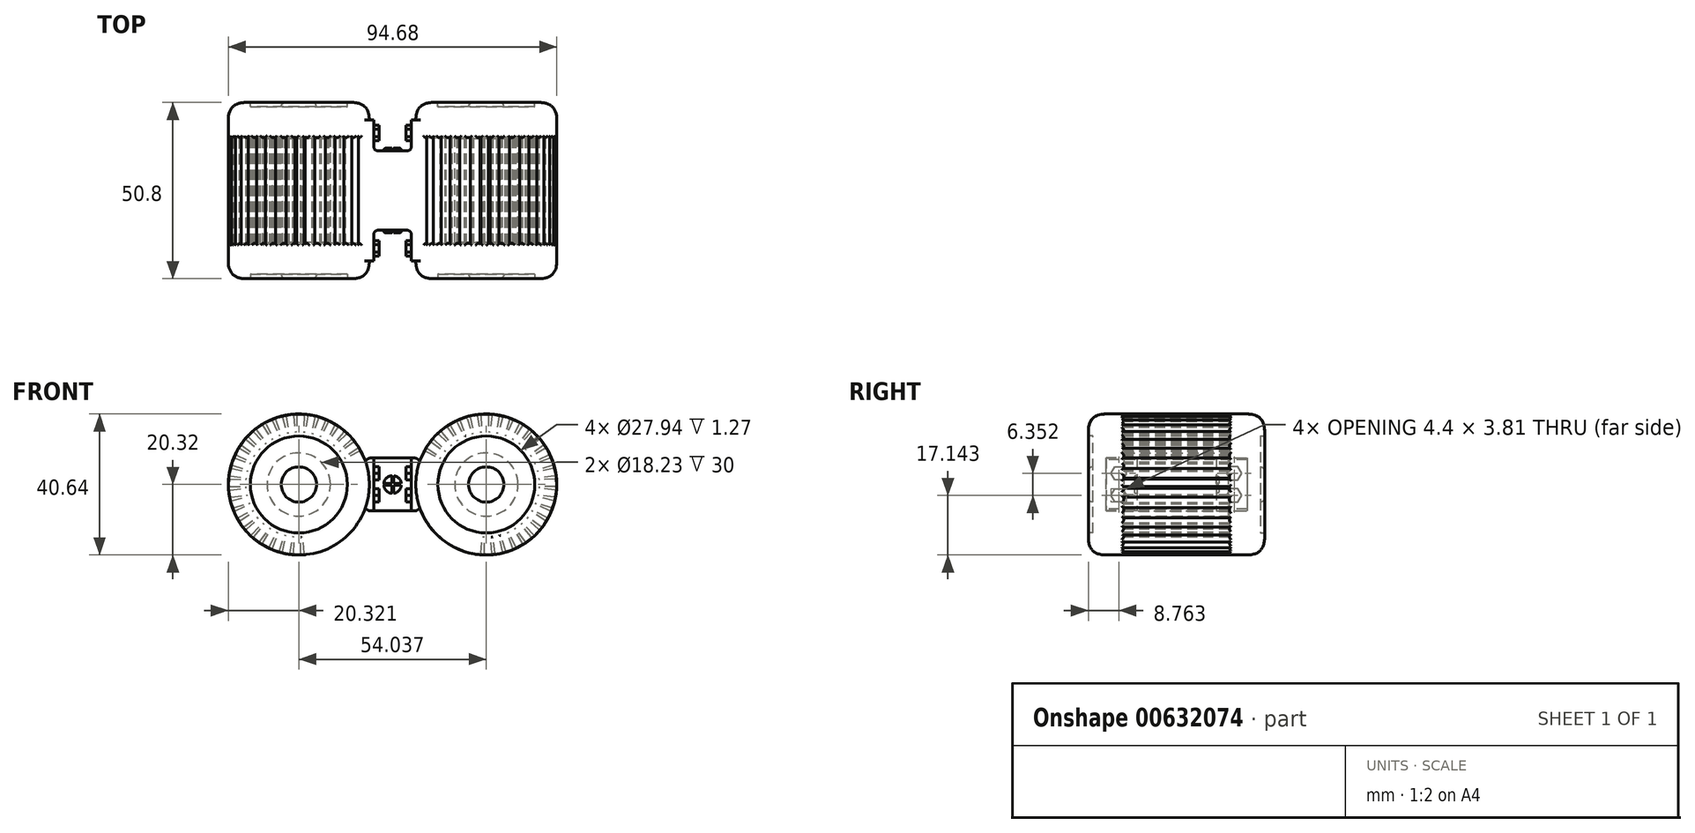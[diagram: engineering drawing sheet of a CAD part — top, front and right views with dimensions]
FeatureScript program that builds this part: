
annotation { "Feature Type Name" : "Feature", "Feature Type Description" : "" }
export const myFeature = defineFeature(function(context is Context, id is Id, definition is map)
    precondition{}
    {
        {
            var Q0;
            Q0=qCreatedBy(makeId("Front.planeOp"),FACE);
            var sketch = newSketch(context, id + "F0", { "sketchPlane" : qUnion([Q0])});
            skArc(sketch, "E0", {"start": v(26.53, 38.5) * mm, "mid": v(31.42, 78.66) * mm, "end": v(18.88, 40.2) * mm});
            skCircle(sketch, "E1", {"center": v(-27.02, 58.82) * mm, "radius": 20.32 * mm});
            skArc(sketch, "E2", {"start": v(18.88, 40.2) * mm, "mid": v(22.62, 38.98) * mm, "end": v(26.53, 38.5) * mm});
            skSolve(sketch);
        }
        {
            var Q0;
            Q0=qSketchRegion(id+"F0",true);
            extrude(context, id + "F1", {"entities" : qUnion([Q0]), "endBound" : BoundingType.SYMMETRIC, "depth" : 50.8 * mm});
        }
        {
            var Q0;
            Q0=qCreatedBy(makeId("Front.planeOp"),FACE);
            var sketch = newSketch(context, id + "F2", { "sketchPlane" : qUnion([Q0])});
            skLineSegment(sketch, "E3.1.0", {"start": v(13.83, 74.28) * mm, "end": v(17.03, 70.33) * mm});
            skLineSegment(sketch, "E3.1.1", {"start": v(13.07, 73.6) * mm, "end": v(16.65, 69.99) * mm});
            skLineSegment(sketch, "E3.1.2", {"start": v(13.07, 73.6) * mm, "end": v(13.83, 74.28) * mm});
            skLineSegment(sketch, "E3.1.3", {"start": v(16.65, 69.99) * mm, "end": v(17.03, 70.33) * mm, "construction": true});
            skLineSegment(sketch, "E3.1.4", {"start": v(16.65, 69.99) * mm, "end": v(17.03, 70.33) * mm});
            skPoint(sketch, "E4", {"position": v(27.02, 58.82) * mm});
            skPoint(sketch, "E5", {"position": v(-27.02, 58.82) * mm});
            skLineSegment(sketch, "E6", {"start": v(27.02, 58.82) * mm, "end": v(13.45, 73.94) * mm, "construction": true});
            skLineSegment(sketch, "E7.1.0", {"start": v(-13.07, 73.6) * mm, "end": v(-16.65, 69.99) * mm});
            skLineSegment(sketch, "E7.1.1", {"start": v(-13.83, 74.28) * mm, "end": v(-17.03, 70.33) * mm});
            skLineSegment(sketch, "E7.1.2", {"start": v(-13.83, 74.28) * mm, "end": v(-13.07, 73.6) * mm});
            skLineSegment(sketch, "E7.1.3", {"start": v(-17.03, 70.33) * mm, "end": v(-16.65, 69.99) * mm, "construction": true});
            skLineSegment(sketch, "E7.1.4", {"start": v(-17.03, 70.33) * mm, "end": v(-16.65, 69.99) * mm});
            skLineSegment(sketch, "E8", {"start": v(-27.02, 58.82) * mm, "end": v(-13.45, 73.94) * mm, "construction": true});
            skLineSegment(sketch, "E9.1.0", {"start": v(11.57, 72.03) * mm, "end": v(15.35, 68.63) * mm});
            skLineSegment(sketch, "E9.1.1", {"start": v(10.93, 71.24) * mm, "end": v(15.03, 68.23) * mm});
            skLineSegment(sketch, "E9.1.2", {"start": v(10.93, 71.24) * mm, "end": v(11.57, 72.03) * mm});
            skLineSegment(sketch, "E9.1.3", {"start": v(15.03, 68.23) * mm, "end": v(15.35, 68.63) * mm, "construction": true});
            skLineSegment(sketch, "E9.1.4", {"start": v(15.03, 68.23) * mm, "end": v(15.35, 68.63) * mm});
            skLineSegment(sketch, "E9.2.0", {"start": v(9.7, 69.45) * mm, "end": v(13.96, 66.68) * mm});
            skLineSegment(sketch, "E9.2.1", {"start": v(9.18, 68.57) * mm, "end": v(13.7, 66.24) * mm});
            skLineSegment(sketch, "E9.2.2", {"start": v(9.18, 68.57) * mm, "end": v(9.7, 69.45) * mm});
            skLineSegment(sketch, "E9.2.3", {"start": v(13.7, 66.24) * mm, "end": v(13.96, 66.68) * mm, "construction": true});
            skLineSegment(sketch, "E9.2.4", {"start": v(13.7, 66.24) * mm, "end": v(13.96, 66.68) * mm});
            skLineSegment(sketch, "E9.15.0", {"start": v(25.41, 38.55) * mm, "end": v(25.94, 43.62) * mm});
            skLineSegment(sketch, "E9.15.1", {"start": v(26.43, 38.5) * mm, "end": v(26.45, 43.59) * mm});
            skLineSegment(sketch, "E9.15.2", {"start": v(26.43, 38.5) * mm, "end": v(25.41, 38.55) * mm});
            skLineSegment(sketch, "E9.15.3", {"start": v(26.45, 43.59) * mm, "end": v(25.94, 43.62) * mm, "construction": true});
            skLineSegment(sketch, "E9.15.4", {"start": v(26.45, 43.59) * mm, "end": v(25.94, 43.62) * mm});
            skLineSegment(sketch, "E9.16.0", {"start": v(28.6, 38.55) * mm, "end": v(28.33, 43.63) * mm});
            skLineSegment(sketch, "E9.16.1", {"start": v(29.61, 38.66) * mm, "end": v(28.84, 43.69) * mm});
            skLineSegment(sketch, "E9.16.2", {"start": v(29.61, 38.66) * mm, "end": v(28.6, 38.55) * mm});
            skLineSegment(sketch, "E9.16.3", {"start": v(28.84, 43.69) * mm, "end": v(28.33, 43.63) * mm, "construction": true});
            skLineSegment(sketch, "E9.16.4", {"start": v(28.84, 43.69) * mm, "end": v(28.33, 43.63) * mm});
            skLineSegment(sketch, "E9.17.0", {"start": v(31.75, 39.05) * mm, "end": v(30.7, 44.03) * mm});
            skLineSegment(sketch, "E9.17.1", {"start": v(32.73, 39.31) * mm, "end": v(31.18, 44.16) * mm});
            skLineSegment(sketch, "E9.17.2", {"start": v(32.73, 39.31) * mm, "end": v(31.75, 39.05) * mm});
            skLineSegment(sketch, "E9.17.3", {"start": v(31.18, 44.16) * mm, "end": v(30.7, 44.03) * mm, "construction": true});
            skLineSegment(sketch, "E9.17.4", {"start": v(31.18, 44.16) * mm, "end": v(30.7, 44.03) * mm});
            skLineSegment(sketch, "E9.18.0", {"start": v(34.79, 40.03) * mm, "end": v(32.96, 44.78) * mm});
            skLineSegment(sketch, "E9.18.1", {"start": v(35.72, 40.45) * mm, "end": v(33.42, 44.99) * mm});
            skLineSegment(sketch, "E9.18.2", {"start": v(35.72, 40.45) * mm, "end": v(34.79, 40.03) * mm});
            skLineSegment(sketch, "E9.18.3", {"start": v(33.42, 44.99) * mm, "end": v(32.96, 44.78) * mm, "construction": true});
            skLineSegment(sketch, "E9.18.4", {"start": v(33.42, 44.99) * mm, "end": v(32.96, 44.78) * mm});
            skLineSegment(sketch, "E9.19.0", {"start": v(37.63, 41.48) * mm, "end": v(35.08, 45.89) * mm});
            skLineSegment(sketch, "E9.19.1", {"start": v(38.48, 42.03) * mm, "end": v(35.5, 46.16) * mm});
            skLineSegment(sketch, "E9.19.2", {"start": v(38.48, 42.03) * mm, "end": v(37.63, 41.48) * mm});
            skLineSegment(sketch, "E9.19.3", {"start": v(35.5, 46.16) * mm, "end": v(35.08, 45.89) * mm, "construction": true});
            skLineSegment(sketch, "E9.19.4", {"start": v(35.5, 46.16) * mm, "end": v(35.08, 45.89) * mm});
            skLineSegment(sketch, "E9.20.0", {"start": v(40.21, 43.35) * mm, "end": v(37, 47.3) * mm});
            skLineSegment(sketch, "E9.20.1", {"start": v(40.97, 44.03) * mm, "end": v(37.38, 47.65) * mm});
            skLineSegment(sketch, "E9.20.2", {"start": v(40.97, 44.03) * mm, "end": v(40.21, 43.35) * mm});
            skLineSegment(sketch, "E9.20.3", {"start": v(37.38, 47.65) * mm, "end": v(37, 47.3) * mm, "construction": true});
            skLineSegment(sketch, "E9.20.4", {"start": v(37.38, 47.65) * mm, "end": v(37, 47.3) * mm});
            skLineSegment(sketch, "E9.21.0", {"start": v(42.47, 45.6) * mm, "end": v(38.68, 49.01) * mm});
            skLineSegment(sketch, "E9.21.1", {"start": v(43.1, 46.4) * mm, "end": v(39, 49.4) * mm});
            skLineSegment(sketch, "E9.21.2", {"start": v(43.1, 46.4) * mm, "end": v(42.47, 45.6) * mm});
            skLineSegment(sketch, "E9.21.3", {"start": v(39, 49.4) * mm, "end": v(38.68, 49.01) * mm, "construction": true});
            skLineSegment(sketch, "E9.21.4", {"start": v(39, 49.4) * mm, "end": v(38.68, 49.01) * mm});
            skLineSegment(sketch, "E9.22.0", {"start": v(44.34, 48.19) * mm, "end": v(40.07, 50.96) * mm});
            skLineSegment(sketch, "E9.22.1", {"start": v(44.85, 49.07) * mm, "end": v(40.33, 51.4) * mm});
            skLineSegment(sketch, "E9.22.2", {"start": v(44.85, 49.07) * mm, "end": v(44.34, 48.19) * mm});
            skLineSegment(sketch, "E9.22.3", {"start": v(40.33, 51.4) * mm, "end": v(40.07, 50.96) * mm, "construction": true});
            skLineSegment(sketch, "E9.22.4", {"start": v(40.33, 51.4) * mm, "end": v(40.07, 50.96) * mm});
            skLineSegment(sketch, "E9.23.0", {"start": v(45.8, 51.03) * mm, "end": v(41.14, 53.1) * mm});
            skLineSegment(sketch, "E9.23.1", {"start": v(46.16, 51.98) * mm, "end": v(41.33, 53.57) * mm});
            skLineSegment(sketch, "E9.23.2", {"start": v(46.16, 51.98) * mm, "end": v(45.8, 51.03) * mm});
            skLineSegment(sketch, "E9.23.3", {"start": v(41.33, 53.57) * mm, "end": v(41.14, 53.1) * mm, "construction": true});
            skLineSegment(sketch, "E9.23.4", {"start": v(41.33, 53.57) * mm, "end": v(41.14, 53.1) * mm});
            skLineSegment(sketch, "E9.24.0", {"start": v(46.78, 54.06) * mm, "end": v(41.86, 55.37) * mm});
            skLineSegment(sketch, "E9.24.1", {"start": v(47, 55.05) * mm, "end": v(41.97, 55.87) * mm});
            skLineSegment(sketch, "E9.24.2", {"start": v(47, 55.05) * mm, "end": v(46.78, 54.06) * mm});
            skLineSegment(sketch, "E9.24.3", {"start": v(41.97, 55.87) * mm, "end": v(41.86, 55.37) * mm, "construction": true});
            skLineSegment(sketch, "E9.24.4", {"start": v(41.97, 55.87) * mm, "end": v(41.86, 55.37) * mm});
            skLineSegment(sketch, "E9.25.0", {"start": v(47.28, 57.21) * mm, "end": v(42.22, 57.74) * mm});
            skLineSegment(sketch, "E9.25.1", {"start": v(47.34, 58.23) * mm, "end": v(42.25, 58.25) * mm});
            skLineSegment(sketch, "E9.25.2", {"start": v(47.34, 58.23) * mm, "end": v(47.28, 57.21) * mm});
            skLineSegment(sketch, "E9.25.3", {"start": v(42.25, 58.25) * mm, "end": v(42.22, 57.74) * mm, "construction": true});
            skLineSegment(sketch, "E9.25.4", {"start": v(42.25, 58.25) * mm, "end": v(42.22, 57.74) * mm});
            skLineSegment(sketch, "E9.26.0", {"start": v(47.28, 60.4) * mm, "end": v(42.2, 60.13) * mm});
            skLineSegment(sketch, "E9.26.1", {"start": v(47.18, 61.41) * mm, "end": v(42.15, 60.64) * mm});
            skLineSegment(sketch, "E9.26.2", {"start": v(47.18, 61.41) * mm, "end": v(47.28, 60.4) * mm});
            skLineSegment(sketch, "E9.26.3", {"start": v(42.15, 60.64) * mm, "end": v(42.2, 60.13) * mm, "construction": true});
            skLineSegment(sketch, "E9.26.4", {"start": v(42.15, 60.64) * mm, "end": v(42.2, 60.13) * mm});
            skLineSegment(sketch, "E9.27.0", {"start": v(46.79, 63.55) * mm, "end": v(41.8, 62.5) * mm});
            skLineSegment(sketch, "E9.27.1", {"start": v(46.52, 64.53) * mm, "end": v(41.68, 62.98) * mm});
            skLineSegment(sketch, "E9.27.2", {"start": v(46.52, 64.53) * mm, "end": v(46.79, 63.55) * mm});
            skLineSegment(sketch, "E9.27.3", {"start": v(41.68, 62.98) * mm, "end": v(41.8, 62.5) * mm, "construction": true});
            skLineSegment(sketch, "E9.27.4", {"start": v(41.68, 62.98) * mm, "end": v(41.8, 62.5) * mm});
            skLineSegment(sketch, "E9.28.0", {"start": v(45.8, 66.59) * mm, "end": v(41.05, 64.76) * mm});
            skLineSegment(sketch, "E9.28.1", {"start": v(45.4, 67.51) * mm, "end": v(40.85, 65.22) * mm});
            skLineSegment(sketch, "E9.28.2", {"start": v(45.4, 67.51) * mm, "end": v(45.8, 66.59) * mm});
            skLineSegment(sketch, "E9.28.3", {"start": v(40.85, 65.22) * mm, "end": v(41.05, 64.76) * mm, "construction": true});
            skLineSegment(sketch, "E9.28.4", {"start": v(40.85, 65.22) * mm, "end": v(41.05, 64.76) * mm});
            skLineSegment(sketch, "E9.29.0", {"start": v(44.36, 69.43) * mm, "end": v(39.95, 66.88) * mm});
            skLineSegment(sketch, "E9.29.1", {"start": v(43.8, 70.28) * mm, "end": v(39.67, 67.3) * mm});
            skLineSegment(sketch, "E9.29.2", {"start": v(43.8, 70.28) * mm, "end": v(44.36, 69.43) * mm});
            skLineSegment(sketch, "E9.29.3", {"start": v(39.67, 67.3) * mm, "end": v(39.95, 66.88) * mm, "construction": true});
            skLineSegment(sketch, "E9.29.4", {"start": v(39.67, 67.3) * mm, "end": v(39.95, 66.88) * mm});
            skLineSegment(sketch, "E9.30.0", {"start": v(42.48, 72) * mm, "end": v(38.53, 68.8) * mm});
            skLineSegment(sketch, "E9.30.1", {"start": v(41.8, 72.77) * mm, "end": v(38.2, 69.18) * mm});
            skLineSegment(sketch, "E9.30.2", {"start": v(41.8, 72.77) * mm, "end": v(42.48, 72) * mm});
            skLineSegment(sketch, "E9.30.3", {"start": v(38.2, 69.18) * mm, "end": v(38.53, 68.8) * mm, "construction": true});
            skLineSegment(sketch, "E9.30.4", {"start": v(38.2, 69.18) * mm, "end": v(38.53, 68.8) * mm});
            skLineSegment(sketch, "E9.31.0", {"start": v(40.23, 74.27) * mm, "end": v(36.83, 70.48) * mm});
            skLineSegment(sketch, "E9.31.1", {"start": v(39.44, 74.9) * mm, "end": v(36.43, 70.8) * mm});
            skLineSegment(sketch, "E9.31.2", {"start": v(39.44, 74.9) * mm, "end": v(40.23, 74.27) * mm});
            skLineSegment(sketch, "E9.31.3", {"start": v(36.43, 70.8) * mm, "end": v(36.83, 70.48) * mm, "construction": true});
            skLineSegment(sketch, "E9.31.4", {"start": v(36.43, 70.8) * mm, "end": v(36.83, 70.48) * mm});
            skLineSegment(sketch, "E9.32.0", {"start": v(37.65, 76.14) * mm, "end": v(34.88, 71.87) * mm});
            skLineSegment(sketch, "E9.32.1", {"start": v(36.77, 76.65) * mm, "end": v(34.44, 72.13) * mm});
            skLineSegment(sketch, "E9.32.2", {"start": v(36.77, 76.65) * mm, "end": v(37.65, 76.14) * mm});
            skLineSegment(sketch, "E9.32.3", {"start": v(34.44, 72.13) * mm, "end": v(34.88, 71.87) * mm, "construction": true});
            skLineSegment(sketch, "E9.32.4", {"start": v(34.44, 72.13) * mm, "end": v(34.88, 71.87) * mm});
            skLineSegment(sketch, "E9.33.0", {"start": v(34.8, 77.6) * mm, "end": v(32.74, 72.94) * mm});
            skLineSegment(sketch, "E9.33.1", {"start": v(33.86, 77.96) * mm, "end": v(32.27, 73.13) * mm});
            skLineSegment(sketch, "E9.33.2", {"start": v(33.86, 77.96) * mm, "end": v(34.8, 77.6) * mm});
            skLineSegment(sketch, "E9.33.3", {"start": v(32.27, 73.13) * mm, "end": v(32.74, 72.94) * mm, "construction": true});
            skLineSegment(sketch, "E9.33.4", {"start": v(32.27, 73.13) * mm, "end": v(32.74, 72.94) * mm});
            skLineSegment(sketch, "E9.34.0", {"start": v(31.78, 78.58) * mm, "end": v(30.46, 73.66) * mm});
            skLineSegment(sketch, "E9.34.1", {"start": v(30.78, 78.8) * mm, "end": v(29.96, 73.77) * mm});
            skLineSegment(sketch, "E9.34.2", {"start": v(30.78, 78.8) * mm, "end": v(31.78, 78.58) * mm});
            skLineSegment(sketch, "E9.34.3", {"start": v(29.96, 73.77) * mm, "end": v(30.46, 73.66) * mm, "construction": true});
            skLineSegment(sketch, "E9.34.4", {"start": v(29.96, 73.77) * mm, "end": v(30.46, 73.66) * mm});
            skLineSegment(sketch, "E9.35.0", {"start": v(28.63, 79.08) * mm, "end": v(28.1, 74.02) * mm});
            skLineSegment(sketch, "E9.35.1", {"start": v(27.61, 79.14) * mm, "end": v(27.59, 74.05) * mm});
            skLineSegment(sketch, "E9.35.2", {"start": v(27.61, 79.14) * mm, "end": v(28.63, 79.08) * mm});
            skLineSegment(sketch, "E9.35.3", {"start": v(27.59, 74.05) * mm, "end": v(28.1, 74.02) * mm, "construction": true});
            skLineSegment(sketch, "E9.35.4", {"start": v(27.59, 74.05) * mm, "end": v(28.1, 74.02) * mm});
            skLineSegment(sketch, "E9.36.0", {"start": v(25.44, 79.08) * mm, "end": v(25.7, 74) * mm});
            skLineSegment(sketch, "E9.36.1", {"start": v(24.42, 78.98) * mm, "end": v(25.2, 73.95) * mm});
            skLineSegment(sketch, "E9.36.2", {"start": v(24.42, 78.98) * mm, "end": v(25.44, 79.08) * mm});
            skLineSegment(sketch, "E9.36.3", {"start": v(25.2, 73.95) * mm, "end": v(25.7, 74) * mm, "construction": true});
            skLineSegment(sketch, "E9.36.4", {"start": v(25.2, 73.95) * mm, "end": v(25.7, 74) * mm});
            skLineSegment(sketch, "E9.37.0", {"start": v(22.28, 78.59) * mm, "end": v(23.35, 73.6) * mm});
            skLineSegment(sketch, "E9.37.1", {"start": v(21.3, 78.32) * mm, "end": v(22.86, 73.48) * mm});
            skLineSegment(sketch, "E9.37.2", {"start": v(21.3, 78.32) * mm, "end": v(22.28, 78.59) * mm});
            skLineSegment(sketch, "E9.37.3", {"start": v(22.86, 73.48) * mm, "end": v(23.35, 73.6) * mm, "construction": true});
            skLineSegment(sketch, "E9.37.4", {"start": v(22.86, 73.48) * mm, "end": v(23.35, 73.6) * mm});
            skLineSegment(sketch, "E9.38.0", {"start": v(19.25, 77.6) * mm, "end": v(21.08, 72.85) * mm});
            skLineSegment(sketch, "E9.38.1", {"start": v(18.32, 77.19) * mm, "end": v(20.61, 72.65) * mm});
            skLineSegment(sketch, "E9.38.2", {"start": v(18.32, 77.19) * mm, "end": v(19.25, 77.6) * mm});
            skLineSegment(sketch, "E9.38.3", {"start": v(20.61, 72.65) * mm, "end": v(21.08, 72.85) * mm, "construction": true});
            skLineSegment(sketch, "E9.38.4", {"start": v(20.61, 72.65) * mm, "end": v(21.08, 72.85) * mm});
            skLineSegment(sketch, "E9.39.0", {"start": v(16.4, 76.15) * mm, "end": v(18.96, 71.75) * mm});
            skLineSegment(sketch, "E9.39.1", {"start": v(15.56, 75.6) * mm, "end": v(18.53, 71.47) * mm});
            skLineSegment(sketch, "E9.39.2", {"start": v(15.56, 75.6) * mm, "end": v(16.4, 76.15) * mm});
            skLineSegment(sketch, "E9.39.3", {"start": v(18.53, 71.47) * mm, "end": v(18.96, 71.75) * mm, "construction": true});
            skLineSegment(sketch, "E9.39.4", {"start": v(18.53, 71.47) * mm, "end": v(18.96, 71.75) * mm});
            skLineSegment(sketch, "E10.1.0", {"start": v(-15.56, 75.6) * mm, "end": v(-18.53, 71.47) * mm});
            skLineSegment(sketch, "E10.1.1", {"start": v(-16.4, 76.15) * mm, "end": v(-18.96, 71.75) * mm});
            skLineSegment(sketch, "E10.1.2", {"start": v(-16.4, 76.15) * mm, "end": v(-15.56, 75.6) * mm});
            skLineSegment(sketch, "E10.1.3", {"start": v(-18.96, 71.75) * mm, "end": v(-18.53, 71.47) * mm, "construction": true});
            skLineSegment(sketch, "E10.1.4", {"start": v(-18.96, 71.75) * mm, "end": v(-18.53, 71.47) * mm});
            skLineSegment(sketch, "E10.2.0", {"start": v(-18.32, 77.19) * mm, "end": v(-20.61, 72.65) * mm});
            skLineSegment(sketch, "E10.2.1", {"start": v(-19.25, 77.6) * mm, "end": v(-21.08, 72.85) * mm});
            skLineSegment(sketch, "E10.2.2", {"start": v(-19.25, 77.6) * mm, "end": v(-18.32, 77.19) * mm});
            skLineSegment(sketch, "E10.2.3", {"start": v(-21.08, 72.85) * mm, "end": v(-20.61, 72.65) * mm, "construction": true});
            skLineSegment(sketch, "E10.2.4", {"start": v(-21.08, 72.85) * mm, "end": v(-20.61, 72.65) * mm});
            skLineSegment(sketch, "E10.3.0", {"start": v(-21.3, 78.32) * mm, "end": v(-22.86, 73.48) * mm});
            skLineSegment(sketch, "E10.3.1", {"start": v(-22.28, 78.59) * mm, "end": v(-23.35, 73.6) * mm});
            skLineSegment(sketch, "E10.3.2", {"start": v(-22.28, 78.59) * mm, "end": v(-21.3, 78.32) * mm});
            skLineSegment(sketch, "E10.3.3", {"start": v(-23.35, 73.6) * mm, "end": v(-22.86, 73.48) * mm, "construction": true});
            skLineSegment(sketch, "E10.3.4", {"start": v(-23.35, 73.6) * mm, "end": v(-22.86, 73.48) * mm});
            skLineSegment(sketch, "E10.4.0", {"start": v(-24.42, 78.98) * mm, "end": v(-25.2, 73.95) * mm});
            skLineSegment(sketch, "E10.4.1", {"start": v(-25.44, 79.08) * mm, "end": v(-25.7, 74) * mm});
            skLineSegment(sketch, "E10.4.2", {"start": v(-25.44, 79.08) * mm, "end": v(-24.42, 78.98) * mm});
            skLineSegment(sketch, "E10.4.3", {"start": v(-25.7, 74) * mm, "end": v(-25.2, 73.95) * mm, "construction": true});
            skLineSegment(sketch, "E10.4.4", {"start": v(-25.7, 74) * mm, "end": v(-25.2, 73.95) * mm});
            skLineSegment(sketch, "E10.5.0", {"start": v(-27.61, 79.14) * mm, "end": v(-27.59, 74.05) * mm});
            skLineSegment(sketch, "E10.5.1", {"start": v(-28.63, 79.08) * mm, "end": v(-28.1, 74.02) * mm});
            skLineSegment(sketch, "E10.5.2", {"start": v(-28.63, 79.08) * mm, "end": v(-27.61, 79.14) * mm});
            skLineSegment(sketch, "E10.5.3", {"start": v(-28.1, 74.02) * mm, "end": v(-27.59, 74.05) * mm, "construction": true});
            skLineSegment(sketch, "E10.5.4", {"start": v(-28.1, 74.02) * mm, "end": v(-27.59, 74.05) * mm});
            skLineSegment(sketch, "E10.6.0", {"start": v(-30.78, 78.8) * mm, "end": v(-29.96, 73.77) * mm});
            skLineSegment(sketch, "E10.6.1", {"start": v(-31.78, 78.58) * mm, "end": v(-30.46, 73.66) * mm});
            skLineSegment(sketch, "E10.6.2", {"start": v(-31.78, 78.58) * mm, "end": v(-30.78, 78.8) * mm});
            skLineSegment(sketch, "E10.6.3", {"start": v(-30.46, 73.66) * mm, "end": v(-29.96, 73.77) * mm, "construction": true});
            skLineSegment(sketch, "E10.6.4", {"start": v(-30.46, 73.66) * mm, "end": v(-29.96, 73.77) * mm});
            skLineSegment(sketch, "E10.7.0", {"start": v(-33.86, 77.96) * mm, "end": v(-32.27, 73.13) * mm});
            skLineSegment(sketch, "E10.7.1", {"start": v(-34.8, 77.6) * mm, "end": v(-32.74, 72.94) * mm});
            skLineSegment(sketch, "E10.7.2", {"start": v(-34.8, 77.6) * mm, "end": v(-33.86, 77.96) * mm});
            skLineSegment(sketch, "E10.7.3", {"start": v(-32.74, 72.94) * mm, "end": v(-32.27, 73.13) * mm, "construction": true});
            skLineSegment(sketch, "E10.7.4", {"start": v(-32.74, 72.94) * mm, "end": v(-32.27, 73.13) * mm});
            skLineSegment(sketch, "E10.8.0", {"start": v(-36.77, 76.65) * mm, "end": v(-34.44, 72.13) * mm});
            skLineSegment(sketch, "E10.8.1", {"start": v(-37.65, 76.14) * mm, "end": v(-34.88, 71.87) * mm});
            skLineSegment(sketch, "E10.8.2", {"start": v(-37.65, 76.14) * mm, "end": v(-36.77, 76.65) * mm});
            skLineSegment(sketch, "E10.8.3", {"start": v(-34.88, 71.87) * mm, "end": v(-34.44, 72.13) * mm, "construction": true});
            skLineSegment(sketch, "E10.8.4", {"start": v(-34.88, 71.87) * mm, "end": v(-34.44, 72.13) * mm});
            skLineSegment(sketch, "E10.9.0", {"start": v(-39.44, 74.9) * mm, "end": v(-36.43, 70.8) * mm});
            skLineSegment(sketch, "E10.9.1", {"start": v(-40.23, 74.27) * mm, "end": v(-36.83, 70.48) * mm});
            skLineSegment(sketch, "E10.9.2", {"start": v(-40.23, 74.27) * mm, "end": v(-39.44, 74.9) * mm});
            skLineSegment(sketch, "E10.9.3", {"start": v(-36.83, 70.48) * mm, "end": v(-36.43, 70.8) * mm, "construction": true});
            skLineSegment(sketch, "E10.9.4", {"start": v(-36.83, 70.48) * mm, "end": v(-36.43, 70.8) * mm});
            skLineSegment(sketch, "E10.10.0", {"start": v(-41.8, 72.77) * mm, "end": v(-38.2, 69.18) * mm});
            skLineSegment(sketch, "E10.10.1", {"start": v(-42.48, 72) * mm, "end": v(-38.53, 68.8) * mm});
            skLineSegment(sketch, "E10.10.2", {"start": v(-42.48, 72) * mm, "end": v(-41.8, 72.77) * mm});
            skLineSegment(sketch, "E10.10.3", {"start": v(-38.53, 68.8) * mm, "end": v(-38.2, 69.18) * mm, "construction": true});
            skLineSegment(sketch, "E10.10.4", {"start": v(-38.53, 68.8) * mm, "end": v(-38.2, 69.18) * mm});
            skLineSegment(sketch, "E10.11.0", {"start": v(-43.8, 70.28) * mm, "end": v(-39.67, 67.3) * mm});
            skLineSegment(sketch, "E10.11.1", {"start": v(-44.36, 69.43) * mm, "end": v(-39.95, 66.88) * mm});
            skLineSegment(sketch, "E10.11.2", {"start": v(-44.36, 69.43) * mm, "end": v(-43.8, 70.28) * mm});
            skLineSegment(sketch, "E10.11.3", {"start": v(-39.95, 66.88) * mm, "end": v(-39.67, 67.3) * mm, "construction": true});
            skLineSegment(sketch, "E10.11.4", {"start": v(-39.95, 66.88) * mm, "end": v(-39.67, 67.3) * mm});
            skLineSegment(sketch, "E10.12.0", {"start": v(-45.4, 67.51) * mm, "end": v(-40.85, 65.22) * mm});
            skLineSegment(sketch, "E10.12.1", {"start": v(-45.8, 66.59) * mm, "end": v(-41.05, 64.76) * mm});
            skLineSegment(sketch, "E10.12.2", {"start": v(-45.8, 66.59) * mm, "end": v(-45.4, 67.51) * mm});
            skLineSegment(sketch, "E10.12.3", {"start": v(-41.05, 64.76) * mm, "end": v(-40.85, 65.22) * mm, "construction": true});
            skLineSegment(sketch, "E10.12.4", {"start": v(-41.05, 64.76) * mm, "end": v(-40.85, 65.22) * mm});
            skLineSegment(sketch, "E10.13.0", {"start": v(-46.52, 64.53) * mm, "end": v(-41.68, 62.98) * mm});
            skLineSegment(sketch, "E10.13.1", {"start": v(-46.79, 63.55) * mm, "end": v(-41.8, 62.5) * mm});
            skLineSegment(sketch, "E10.13.2", {"start": v(-46.79, 63.55) * mm, "end": v(-46.52, 64.53) * mm});
            skLineSegment(sketch, "E10.13.3", {"start": v(-41.8, 62.5) * mm, "end": v(-41.68, 62.98) * mm, "construction": true});
            skLineSegment(sketch, "E10.13.4", {"start": v(-41.8, 62.5) * mm, "end": v(-41.68, 62.98) * mm});
            skLineSegment(sketch, "E10.14.0", {"start": v(-47.18, 61.41) * mm, "end": v(-42.15, 60.64) * mm});
            skLineSegment(sketch, "E10.14.1", {"start": v(-47.28, 60.4) * mm, "end": v(-42.2, 60.13) * mm});
            skLineSegment(sketch, "E10.14.2", {"start": v(-47.28, 60.4) * mm, "end": v(-47.18, 61.41) * mm});
            skLineSegment(sketch, "E10.14.3", {"start": v(-42.2, 60.13) * mm, "end": v(-42.15, 60.64) * mm, "construction": true});
            skLineSegment(sketch, "E10.14.4", {"start": v(-42.2, 60.13) * mm, "end": v(-42.15, 60.64) * mm});
            skLineSegment(sketch, "E10.15.0", {"start": v(-47.34, 58.23) * mm, "end": v(-42.25, 58.25) * mm});
            skLineSegment(sketch, "E10.15.1", {"start": v(-47.28, 57.21) * mm, "end": v(-42.22, 57.74) * mm});
            skLineSegment(sketch, "E10.15.2", {"start": v(-47.28, 57.21) * mm, "end": v(-47.34, 58.23) * mm});
            skLineSegment(sketch, "E10.15.3", {"start": v(-42.22, 57.74) * mm, "end": v(-42.25, 58.25) * mm, "construction": true});
            skLineSegment(sketch, "E10.15.4", {"start": v(-42.22, 57.74) * mm, "end": v(-42.25, 58.25) * mm});
            skLineSegment(sketch, "E10.16.0", {"start": v(-47, 55.05) * mm, "end": v(-41.97, 55.87) * mm});
            skLineSegment(sketch, "E10.16.1", {"start": v(-46.78, 54.06) * mm, "end": v(-41.86, 55.37) * mm});
            skLineSegment(sketch, "E10.16.2", {"start": v(-46.78, 54.06) * mm, "end": v(-47, 55.05) * mm});
            skLineSegment(sketch, "E10.16.3", {"start": v(-41.86, 55.37) * mm, "end": v(-41.97, 55.87) * mm, "construction": true});
            skLineSegment(sketch, "E10.16.4", {"start": v(-41.86, 55.37) * mm, "end": v(-41.97, 55.87) * mm});
            skLineSegment(sketch, "E10.17.0", {"start": v(-46.16, 51.98) * mm, "end": v(-41.33, 53.57) * mm});
            skLineSegment(sketch, "E10.17.1", {"start": v(-45.8, 51.03) * mm, "end": v(-41.14, 53.1) * mm});
            skLineSegment(sketch, "E10.17.2", {"start": v(-45.8, 51.03) * mm, "end": v(-46.16, 51.98) * mm});
            skLineSegment(sketch, "E10.17.3", {"start": v(-41.14, 53.1) * mm, "end": v(-41.33, 53.57) * mm, "construction": true});
            skLineSegment(sketch, "E10.17.4", {"start": v(-41.14, 53.1) * mm, "end": v(-41.33, 53.57) * mm});
            skLineSegment(sketch, "E10.18.0", {"start": v(-44.85, 49.07) * mm, "end": v(-40.33, 51.4) * mm});
            skLineSegment(sketch, "E10.18.1", {"start": v(-44.34, 48.19) * mm, "end": v(-40.07, 50.96) * mm});
            skLineSegment(sketch, "E10.18.2", {"start": v(-44.34, 48.19) * mm, "end": v(-44.85, 49.07) * mm});
            skLineSegment(sketch, "E10.18.3", {"start": v(-40.07, 50.96) * mm, "end": v(-40.33, 51.4) * mm, "construction": true});
            skLineSegment(sketch, "E10.18.4", {"start": v(-40.07, 50.96) * mm, "end": v(-40.33, 51.4) * mm});
            skLineSegment(sketch, "E10.19.0", {"start": v(-43.1, 46.4) * mm, "end": v(-39, 49.4) * mm});
            skLineSegment(sketch, "E10.19.1", {"start": v(-42.47, 45.6) * mm, "end": v(-38.68, 49.01) * mm});
            skLineSegment(sketch, "E10.19.2", {"start": v(-42.47, 45.6) * mm, "end": v(-43.1, 46.4) * mm});
            skLineSegment(sketch, "E10.19.3", {"start": v(-38.68, 49.01) * mm, "end": v(-39, 49.4) * mm, "construction": true});
            skLineSegment(sketch, "E10.19.4", {"start": v(-38.68, 49.01) * mm, "end": v(-39, 49.4) * mm});
            skLineSegment(sketch, "E10.20.0", {"start": v(-40.97, 44.03) * mm, "end": v(-37.38, 47.65) * mm});
            skLineSegment(sketch, "E10.20.1", {"start": v(-40.21, 43.35) * mm, "end": v(-37, 47.3) * mm});
            skLineSegment(sketch, "E10.20.2", {"start": v(-40.21, 43.35) * mm, "end": v(-40.97, 44.03) * mm});
            skLineSegment(sketch, "E10.20.3", {"start": v(-37, 47.3) * mm, "end": v(-37.38, 47.65) * mm, "construction": true});
            skLineSegment(sketch, "E10.20.4", {"start": v(-37, 47.3) * mm, "end": v(-37.38, 47.65) * mm});
            skLineSegment(sketch, "E10.21.0", {"start": v(-38.48, 42.03) * mm, "end": v(-35.5, 46.16) * mm});
            skLineSegment(sketch, "E10.21.1", {"start": v(-37.63, 41.48) * mm, "end": v(-35.08, 45.89) * mm});
            skLineSegment(sketch, "E10.21.2", {"start": v(-37.63, 41.48) * mm, "end": v(-38.48, 42.03) * mm});
            skLineSegment(sketch, "E10.21.3", {"start": v(-35.08, 45.89) * mm, "end": v(-35.5, 46.16) * mm, "construction": true});
            skLineSegment(sketch, "E10.21.4", {"start": v(-35.08, 45.89) * mm, "end": v(-35.5, 46.16) * mm});
            skLineSegment(sketch, "E10.22.0", {"start": v(-35.72, 40.45) * mm, "end": v(-33.42, 44.99) * mm});
            skLineSegment(sketch, "E10.22.1", {"start": v(-34.79, 40.03) * mm, "end": v(-32.96, 44.78) * mm});
            skLineSegment(sketch, "E10.22.2", {"start": v(-34.79, 40.03) * mm, "end": v(-35.72, 40.45) * mm});
            skLineSegment(sketch, "E10.22.3", {"start": v(-32.96, 44.78) * mm, "end": v(-33.42, 44.99) * mm, "construction": true});
            skLineSegment(sketch, "E10.22.4", {"start": v(-32.96, 44.78) * mm, "end": v(-33.42, 44.99) * mm});
            skLineSegment(sketch, "E10.23.0", {"start": v(-32.73, 39.31) * mm, "end": v(-31.18, 44.16) * mm});
            skLineSegment(sketch, "E10.23.1", {"start": v(-31.75, 39.05) * mm, "end": v(-30.7, 44.03) * mm});
            skLineSegment(sketch, "E10.23.2", {"start": v(-31.75, 39.05) * mm, "end": v(-32.73, 39.31) * mm});
            skLineSegment(sketch, "E10.23.3", {"start": v(-30.7, 44.03) * mm, "end": v(-31.18, 44.16) * mm, "construction": true});
            skLineSegment(sketch, "E10.23.4", {"start": v(-30.7, 44.03) * mm, "end": v(-31.18, 44.16) * mm});
            skLineSegment(sketch, "E10.24.0", {"start": v(-29.61, 38.66) * mm, "end": v(-28.84, 43.69) * mm});
            skLineSegment(sketch, "E10.24.1", {"start": v(-28.6, 38.55) * mm, "end": v(-28.33, 43.63) * mm});
            skLineSegment(sketch, "E10.24.2", {"start": v(-28.6, 38.55) * mm, "end": v(-29.61, 38.66) * mm});
            skLineSegment(sketch, "E10.24.3", {"start": v(-28.33, 43.63) * mm, "end": v(-28.84, 43.69) * mm, "construction": true});
            skLineSegment(sketch, "E10.24.4", {"start": v(-28.33, 43.63) * mm, "end": v(-28.84, 43.69) * mm});
            skLineSegment(sketch, "E10.25.0", {"start": v(-26.43, 38.5) * mm, "end": v(-26.45, 43.59) * mm});
            skLineSegment(sketch, "E10.25.1", {"start": v(-25.41, 38.55) * mm, "end": v(-25.94, 43.62) * mm});
            skLineSegment(sketch, "E10.25.2", {"start": v(-25.41, 38.55) * mm, "end": v(-26.43, 38.5) * mm});
            skLineSegment(sketch, "E10.25.3", {"start": v(-25.94, 43.62) * mm, "end": v(-26.45, 43.59) * mm, "construction": true});
            skLineSegment(sketch, "E10.25.4", {"start": v(-25.94, 43.62) * mm, "end": v(-26.45, 43.59) * mm});
            skLineSegment(sketch, "E10.38.0", {"start": v(-9.18, 68.57) * mm, "end": v(-13.7, 66.24) * mm});
            skLineSegment(sketch, "E10.38.1", {"start": v(-9.7, 69.45) * mm, "end": v(-13.96, 66.68) * mm});
            skLineSegment(sketch, "E10.38.2", {"start": v(-9.7, 69.45) * mm, "end": v(-9.18, 68.57) * mm});
            skLineSegment(sketch, "E10.38.3", {"start": v(-13.96, 66.68) * mm, "end": v(-13.7, 66.24) * mm, "construction": true});
            skLineSegment(sketch, "E10.38.4", {"start": v(-13.96, 66.68) * mm, "end": v(-13.7, 66.24) * mm});
            skLineSegment(sketch, "E10.39.0", {"start": v(-10.93, 71.24) * mm, "end": v(-15.03, 68.23) * mm});
            skLineSegment(sketch, "E10.39.1", {"start": v(-11.57, 72.03) * mm, "end": v(-15.35, 68.63) * mm});
            skLineSegment(sketch, "E10.39.2", {"start": v(-11.57, 72.03) * mm, "end": v(-10.93, 71.24) * mm});
            skLineSegment(sketch, "E10.39.3", {"start": v(-15.35, 68.63) * mm, "end": v(-15.03, 68.23) * mm, "construction": true});
            skLineSegment(sketch, "E10.39.4", {"start": v(-15.35, 68.63) * mm, "end": v(-15.03, 68.23) * mm});
            skSolve(sketch);
        }
        {
            var Q0;
            Q0=qSketchRegion(id+"F2",true);
            extrude(context, id + "F3", {"entities" : qUnion([Q0]), "operationType" : NewBodyOperationType.REMOVE, "endBound" : BoundingType.SYMMETRIC, "oppositeDirection" : true, "depth" : 30.48 * mm});
        }
        {
            var Q0;
            Q0=makeQuery(id+"F1.opExtrude","CAP_EDGE",EDGE,{"disambiguationData":[OSD([sQuery(id+"F0.wireOp",EDGE,"E0")])],"isStart":false});
            var Q1;
            Q1=makeQuery(id+"F1.opExtrude","CAP_EDGE",EDGE,{"disambiguationData":[OSD([sQuery(id+"F0.wireOp",EDGE,"E0")])],"isStart":true});
            var Q2;
            Q2=makeQuery(id+"F1.opExtrude","CAP_EDGE",EDGE,{"disambiguationData":[OSD([sQuery(id+"F0.wireOp",EDGE,"eJ6pUaNj-pi6J-WJvS-oHvt-8XujmQXpYSx1")])],"isStart":true});
            var Q3;
            Q3=makeQuery(id+"F1.opExtrude","CAP_EDGE",EDGE,{"disambiguationData":[OSD([sQuery(id+"F0.wireOp",EDGE,"eJ6pUaNj-pi6J-WJvS-oHvt-8XujmQXpYSx1")])],"isStart":false});
            var Q4;
            Q4=makeQuery(id+"F1.opExtrude","CAP_EDGE",EDGE,{"disambiguationData":[OSD([sQuery(id+"F0.wireOp",EDGE,"E1")])],"isStart":false});
            var Q5;
            Q5=makeQuery(id+"F1.opExtrude","CAP_EDGE",EDGE,{"disambiguationData":[OSD([sQuery(id+"F0.wireOp",EDGE,"E1")])],"isStart":true});
            fillet(context, id + "F4", {"entities" : qUnion([Q0, Q1, Q2, Q3, Q4, Q5]), "radius" : 5.08 * mm, "tangentPropagation" : true, "rho" : 0.5, "crossSection" : FilletCrossSection.CONIC, "allowEdgeOverflow" : false});
        }
        {
            var Q0;
            Q0=makeQuery(id+"F1.opExtrude","CAP_FACE",FACE,{"disambiguationData":[OSD([sQuery(id+"F0.wireOp",EDGE,"E0"),sQuery(id+"F0.wireOp",EDGE,"E2")])],"isStart":false});
            var sketch = newSketch(context, id + "F5", { "sketchPlane" : qUnion([Q0])});
            skCircle(sketch, "E11", {"center": v(27.02, 58.82) * mm, "radius": 20.32 * mm, "construction": true});
            skCircle(sketch, "E12", {"center": v(-27.02, 58.82) * mm, "radius": 20.32 * mm, "construction": true});
            skCircle(sketch, "E13", {"center": v(-27.02, 58.82) * mm, "radius": 13.97 * mm});
            skCircle(sketch, "E14", {"center": v(27.02, 58.82) * mm, "radius": 13.97 * mm});
            skCircle(sketch, "E15", {"center": v(-27.02, 58.82) * mm, "radius": 5.08 * mm});
            skCircle(sketch, "E16", {"center": v(27.02, 58.82) * mm, "radius": 5.08 * mm});
            skSolve(sketch);
        }
        {
            var Q0;
            Q0=qSketchRegion(id+"F5",true);
            extrude(context, id + "F6", {"entities" : qUnion([Q0]), "operationType" : NewBodyOperationType.REMOVE, "oppositeDirection" : true, "depth" : 1.27 * mm});
        }
        {
            var Q0;
            Q0=makeQuery(id+"F1.opExtrude","CAP_FACE",FACE,{"disambiguationData":[OSD([sQuery(id+"F0.wireOp",EDGE,"E0"),sQuery(id+"F0.wireOp",EDGE,"E2")])],"isStart":true});
            var sketch = newSketch(context, id + "F7", { "sketchPlane" : qUnion([Q0])});
            skCircle(sketch, "E17", {"center": v(-27.02, 58.82) * mm, "radius": 20.32 * mm, "construction": true});
            skCircle(sketch, "E18", {"center": v(27.02, 58.82) * mm, "radius": 20.32 * mm, "construction": true});
            skCircle(sketch, "E19", {"center": v(27.02, 58.82) * mm, "radius": 13.97 * mm});
            skCircle(sketch, "E20", {"center": v(-27.02, 58.82) * mm, "radius": 13.97 * mm});
            skCircle(sketch, "E21", {"center": v(-27.02, 58.82) * mm, "radius": 5.08 * mm});
            skCircle(sketch, "E22", {"center": v(27.02, 58.82) * mm, "radius": 5.08 * mm});
            skSolve(sketch);
        }
        {
            var Q0;
            Q0=qSketchRegion(id+"F7",true);
            extrude(context, id + "F8", {"entities" : qUnion([Q0]), "operationType" : NewBodyOperationType.REMOVE, "oppositeDirection" : true, "depth" : 1.27 * mm});
        }
        {
            var Q0;
            Q0=makeQuery(id+"F6.boolean.opBoolean","COPY",EDGE,{"derivedFrom":makeQuery(id+"F6.opExtrude","CAP_EDGE",EDGE,{"disambiguationData":[OSD([sQuery(id+"F5.wireOp",EDGE,"E15")])],"isStart":true})});
            var Q1;
            Q1=makeQuery(id+"F6.boolean.opBoolean","COPY",EDGE,{"derivedFrom":makeQuery(id+"F6.opExtrude","CAP_EDGE",EDGE,{"disambiguationData":[OSD([sQuery(id+"F5.wireOp",EDGE,"E16")])],"isStart":true})});
            var Q2;
            Q2=makeQuery(id+"F8.boolean.opBoolean","COPY",EDGE,{"derivedFrom":makeQuery(id+"F8.opExtrude","CAP_EDGE",EDGE,{"disambiguationData":[OSD([sQuery(id+"F7.wireOp",EDGE,"E21")])],"isStart":true})});
            var Q3;
            Q3=makeQuery(id+"F8.boolean.opBoolean","COPY",EDGE,{"derivedFrom":makeQuery(id+"F8.opExtrude","CAP_EDGE",EDGE,{"disambiguationData":[OSD([sQuery(id+"F7.wireOp",EDGE,"E22")])],"isStart":true})});
            fillet(context, id + "F9", {"entities" : qUnion([Q0, Q1, Q2, Q3]), "radius" : 1.27 * mm, "tangentPropagation" : true, "allowEdgeOverflow" : false});
        }
        {
            var Q0;
            Q0=qCreatedBy(makeId("Front.planeOp"),FACE);
            var sketch = newSketch(context, id + "F10", { "sketchPlane" : qUnion([Q0])});
            skArc(sketch, "E23.0", {"start": v(7.6, 64.8) * mm, "mid": v(6.7, 58.82) * mm, "end": v(7.6, 52.84) * mm});
            skArc(sketch, "E23.1", {"start": v(-7.6, 52.84) * mm, "mid": v(-6.7, 58.82) * mm, "end": v(-7.6, 64.8) * mm});
            skLineSegment(sketch, "E24", {"start": v(-6.38, 51.2) * mm, "end": v(6.38, 51.2) * mm});
            skLineSegment(sketch, "E25", {"start": v(-6.38, 66.44) * mm, "end": v(6.38, 66.44) * mm});
            skPoint(sketch, "E26.visualSharp", {"position": v(-8.18, 66.44) * mm});
            skArc(sketch, "E26.filletArc", {"start": v(-6.38, 66.44) * mm, "mid": v(-7.4, 65.92) * mm, "end": v(-7.6, 64.8) * mm});
            skPoint(sketch, "E27.visualSharp", {"position": v(8.18, 66.44) * mm});
            skArc(sketch, "E27.filletArc", {"start": v(7.6, 64.8) * mm, "mid": v(7.4, 65.92) * mm, "end": v(6.38, 66.44) * mm});
            skPoint(sketch, "E28.visualSharp", {"position": v(8.18, 51.2) * mm});
            skArc(sketch, "E28.filletArc", {"start": v(6.38, 51.2) * mm, "mid": v(7.4, 51.71) * mm, "end": v(7.6, 52.84) * mm});
            skPoint(sketch, "E29.visualSharp", {"position": v(-8.18, 51.2) * mm});
            skArc(sketch, "E29.filletArc", {"start": v(-7.6, 52.84) * mm, "mid": v(-7.4, 51.71) * mm, "end": v(-6.38, 51.2) * mm});
            skSolve(sketch);
        }
        {
            var Q0;
            Q0=qSketchRegion(id+"F10",true);
            extrude(context, id + "F11", {"entities" : qUnion([Q0]), "depth" : 20.32 * mm});
        }
        {
            var Q0;
            Q0=makeQuery(id+"F11.opExtrude","CAP_FACE",FACE,{"disambiguationData":[OSD([sQuery(id+"F10.wireOp",EDGE,"E23.0"),sQuery(id+"F10.wireOp",EDGE,"E23.1"),sQuery(id+"F10.wireOp",EDGE,"E24"),sQuery(id+"F10.wireOp",EDGE,"E25"),sQuery(id+"F10.wireOp",EDGE,"E26.filletArc"),sQuery(id+"F10.wireOp",EDGE,"E27.filletArc"),sQuery(id+"F10.wireOp",EDGE,"E28.filletArc"),sQuery(id+"F10.wireOp",EDGE,"E29.filletArc")])],"isStart":false});
            var sketch = newSketch(context, id + "F12", { "sketchPlane" : qUnion([Q0])});
            skLineSegment(sketch, "E30.bottom", {"start": v(-5.43, 66.44) * mm, "end": v(5.43, 66.44) * mm});
            skLineSegment(sketch, "E30.top", {"start": v(-5.43, 51.2) * mm, "end": v(5.43, 51.2) * mm});
            skLineSegment(sketch, "E30.left", {"start": v(-5.43, 66.44) * mm, "end": v(-5.43, 51.2) * mm});
            skLineSegment(sketch, "E30.right", {"start": v(5.43, 66.44) * mm, "end": v(5.43, 51.2) * mm});
            skSolve(sketch);
        }
        {
            var Q0;
            Q0=qSketchRegion(id+"F12",true);
            extrude(context, id + "F13", {"entities" : qUnion([Q0]), "operationType" : NewBodyOperationType.REMOVE, "oppositeDirection" : true, "depth" : 8.9 * mm});
        }
        {
            var Q0;
            Q0=makeQuery(id+"F13.boolean.opBoolean","COPY",EDGE,{"derivedFrom":makeQuery(id+"F13.opExtrude","CAP_EDGE",EDGE,{"disambiguationData":[OSD([sQuery(id+"F12.wireOp",EDGE,"E30.left")])],"isStart":false})});
            var Q1;
            Q1=makeQuery(id+"F13.boolean.opBoolean","COPY",EDGE,{"derivedFrom":makeQuery(id+"F13.opExtrude","CAP_EDGE",EDGE,{"disambiguationData":[OSD([sQuery(id+"F12.wireOp",EDGE,"E30.right")])],"isStart":false})});
            fillet(context, id + "F14", {"entities" : qUnion([Q0, Q1]), "radius" : 1.27 * mm, "tangentPropagation" : true, "allowEdgeOverflow" : false});
        }
        {
            var Q0;
            Q0=makeQuery(id+"F13.boolean.opBoolean","COPY",FACE,{"derivedFrom":makeQuery(id+"F13.opExtrude","SWEPT_FACE",FACE,{"disambiguationData":[OSD([sQuery(id+"F12.wireOp",EDGE,"E30.left")])]})});
            var sketch = newSketch(context, id + "F15", { "sketchPlane" : qUnion([Q0])});
            skCircle(sketch, "E31", {"center": v(-16.64, 55.64) * mm, "radius": 1.9 * mm, "construction": true});
            skCircle(sketch, "E32.cCircle", {"center": v(-16.64, 62) * mm, "radius": 1.9 * mm, "construction": true});
            skLineSegment(sketch, "E32.0", {"start": v(-17.74, 63.9) * mm, "end": v(-15.54, 63.9) * mm});
            skLineSegment(sketch, "E32.1", {"start": v(-15.54, 63.9) * mm, "end": v(-14.44, 62) * mm});
            skLineSegment(sketch, "E32.2", {"start": v(-14.44, 62) * mm, "end": v(-15.54, 60.09) * mm});
            skLineSegment(sketch, "E32.3", {"start": v(-15.54, 60.09) * mm, "end": v(-17.74, 60.09) * mm});
            skLineSegment(sketch, "E32.4", {"start": v(-17.74, 60.09) * mm, "end": v(-18.84, 62) * mm});
            skLineSegment(sketch, "E32.5", {"start": v(-18.84, 62) * mm, "end": v(-17.74, 63.9) * mm});
            skPoint(sketch, "E32.0.midPoint", {"position": v(-16.64, 63.9) * mm});
            skLineSegment(sketch, "E33.0", {"start": v(-17.74, 57.55) * mm, "end": v(-15.54, 57.55) * mm});
            skLineSegment(sketch, "E33.1", {"start": v(-15.54, 57.55) * mm, "end": v(-14.44, 55.64) * mm});
            skLineSegment(sketch, "E33.2", {"start": v(-14.44, 55.64) * mm, "end": v(-15.54, 53.74) * mm});
            skLineSegment(sketch, "E33.3", {"start": v(-15.54, 53.74) * mm, "end": v(-17.74, 53.74) * mm});
            skLineSegment(sketch, "E33.4", {"start": v(-17.74, 53.74) * mm, "end": v(-18.84, 55.64) * mm});
            skLineSegment(sketch, "E33.5", {"start": v(-18.84, 55.64) * mm, "end": v(-17.74, 57.55) * mm});
            skPoint(sketch, "E33.0.midPoint", {"position": v(-16.64, 57.55) * mm});
            skSolve(sketch);
        }
        {
            var Q0;
            Q0=qSketchRegion(id+"F15",true);
            extrude(context, id + "F16", {"entities" : qUnion([Q0]), "depth" : 1.52 * mm});
        }
        {
            var Q0;
            Q0=makeQuery(id+"F16.opExtrude","SWEPT_BODY",BODY,{"disambiguationData":[OSD([sQuery(id+"F15.wireOp",EDGE,"E32.0"),sQuery(id+"F15.wireOp",EDGE,"E32.1"),sQuery(id+"F15.wireOp",EDGE,"E32.2"),sQuery(id+"F15.wireOp",EDGE,"E32.3"),sQuery(id+"F15.wireOp",EDGE,"E32.4"),sQuery(id+"F15.wireOp",EDGE,"E32.5")])]});
            var Q1;
            Q1=makeQuery(id+"F16.opExtrude","SWEPT_BODY",BODY,{"disambiguationData":[OSD([sQuery(id+"F15.wireOp",EDGE,"E33.0"),sQuery(id+"F15.wireOp",EDGE,"E33.1"),sQuery(id+"F15.wireOp",EDGE,"E33.2"),sQuery(id+"F15.wireOp",EDGE,"E33.3"),sQuery(id+"F15.wireOp",EDGE,"E33.4"),sQuery(id+"F15.wireOp",EDGE,"E33.5")])]});
            var Q2;
            Q2=qCreatedBy(makeId("Right.planeOp"),FACE);
            mirror(context, id + "F17", {"operationType" : NewBodyOperationType.ADD, "entities" : qUnion([Q0, Q1]), "mirrorPlane" : qUnion([Q2])});
        }
        {
            var Q0;
            Q0=makeQuery(id+"F13.boolean.opBoolean","COPY",FACE,{"derivedFrom":makeQuery(id+"F13.opExtrude","CAP_FACE",FACE,{"disambiguationData":[OSD([sQuery(id+"F12.wireOp",EDGE,"E30.bottom"),sQuery(id+"F12.wireOp",EDGE,"E30.top"),sQuery(id+"F12.wireOp",EDGE,"E30.left"),sQuery(id+"F12.wireOp",EDGE,"E30.right")])],"isStart":false})});
            var sketch = newSketch(context, id + "F18", { "sketchPlane" : qUnion([Q0])});
            skArc(sketch, "E34", {"start": v(-0.25, 61.34) * mm, "mid": v(-1.8, 60.61) * mm, "end": v(-2.53, 59.07) * mm});
            skLineSegment(sketch, "E35.left", {"start": v(-0.25, 61.36) * mm, "end": v(-0.25, 59.07) * mm});
            skLineSegment(sketch, "E35.right", {"start": v(0.25, 61.36) * mm, "end": v(0.25, 59.07) * mm});
            skLineSegment(sketch, "E36.bottom", {"start": v(-2.54, 59.07) * mm, "end": v(-0.25, 59.07) * mm});
            skLineSegment(sketch, "E36.top", {"start": v(-2.54, 58.56) * mm, "end": v(-0.25, 58.56) * mm});
            skLineSegment(sketch, "E37.trimOffspring", {"start": v(0.25, 59.07) * mm, "end": v(2.54, 59.07) * mm});
            skLineSegment(sketch, "E38.trimOffspring", {"start": v(0.25, 58.56) * mm, "end": v(2.54, 58.56) * mm});
            skLineSegment(sketch, "E39.trimOffspring", {"start": v(-0.25, 58.56) * mm, "end": v(-0.25, 56.28) * mm});
            skLineSegment(sketch, "E40.trimOffspring", {"start": v(0.25, 58.56) * mm, "end": v(0.25, 56.28) * mm});
            skArc(sketch, "E41.trimOffspring", {"start": v(-2.53, 58.56) * mm, "mid": v(-1.8, 57.02) * mm, "end": v(-0.25, 56.3) * mm});
            skArc(sketch, "E42.trimOffspring", {"start": v(2.53, 59.07) * mm, "mid": v(1.8, 60.61) * mm, "end": v(0.25, 61.34) * mm});
            skArc(sketch, "E43.trimOffspring", {"start": v(0.25, 56.3) * mm, "mid": v(1.8, 57.02) * mm, "end": v(2.53, 58.56) * mm});
            skSolve(sketch);
        }
        {
            var Q0;
            Q0=qSketchRegion(id+"F18",true);
            extrude(context, id + "F19", {"entities" : qUnion([Q0]), "operationType" : NewBodyOperationType.ADD, "depth" : 0.76 * mm});
        }
        {
            var Q0;
            Q0=makeQuery(id+"F19.opExtrude","CAP_EDGE",EDGE,{"disambiguationData":[OSD([sQuery(id+"F18.wireOp",EDGE,"E42.trimOffspring")])],"isStart":false});
            var Q1;
            Q1=makeQuery(id+"F19.opExtrude","CAP_EDGE",EDGE,{"disambiguationData":[OSD([sQuery(id+"F18.wireOp",EDGE,"E34")])],"isStart":false});
            var Q2;
            Q2=makeQuery(id+"F19.opExtrude","CAP_EDGE",EDGE,{"disambiguationData":[OSD([sQuery(id+"F18.wireOp",EDGE,"E41.trimOffspring")])],"isStart":false});
            var Q3;
            Q3=makeQuery(id+"F19.opExtrude","CAP_EDGE",EDGE,{"disambiguationData":[OSD([sQuery(id+"F18.wireOp",EDGE,"E43.trimOffspring")])],"isStart":false});
            fillet(context, id + "F20", {"entities" : qUnion([Q0, Q1, Q2, Q3]), "radius" : 0.5 * mm, "tangentPropagation" : true, "allowEdgeOverflow" : false});
        }
        {
            var Q0;
            Q0=makeQuery(id+"F11.opExtrude","SWEPT_BODY",BODY,{"disambiguationData":[OSD([sQuery(id+"F10.wireOp",EDGE,"E23.0"),sQuery(id+"F10.wireOp",EDGE,"E23.1"),sQuery(id+"F10.wireOp",EDGE,"E24"),sQuery(id+"F10.wireOp",EDGE,"E25"),sQuery(id+"F10.wireOp",EDGE,"E26.filletArc"),sQuery(id+"F10.wireOp",EDGE,"E27.filletArc"),sQuery(id+"F10.wireOp",EDGE,"E28.filletArc"),sQuery(id+"F10.wireOp",EDGE,"E29.filletArc")])]});
            var Q1;
            Q1=makeQuery(id+"F1.opExtrude","SWEPT_BODY",BODY,{"disambiguationData":[OSD([sQuery(id+"F0.wireOp",EDGE,"E1")])]});
            var Q2;
            Q2=qCreatedBy(makeId("Front.planeOp"),FACE);
            mirror(context, id + "F21", {"operationType" : NewBodyOperationType.ADD, "entities" : qUnion([Q0, Q1]), "mirrorPlane" : qUnion([Q2])});
        }
        {
            var Q0;
            Q0=qCreatedBy(makeId("Front.planeOp"),FACE);
            var sketch = newSketch(context, id + "F22", { "sketchPlane" : qUnion([Q0])});
            skLineSegment(sketch, "E44", {"start": v(0, 58.82) * mm, "end": v(0, 0) * mm, "construction": true});
            skSolve(sketch);
        }
        {
            var Q0;
            Q0=makeQuery(id+"F1.opExtrude","SWEPT_BODY",BODY,{"disambiguationData":[OSD([sQuery(id+"F0.wireOp",EDGE,"E0"),sQuery(id+"F0.wireOp",EDGE,"E2")])]});
            var Q1;
            Q1=sQuery(id+"F22.wireOp",EDGE,"E44");
            transform(context, id + "F23", {"entities" : qUnion([Q0]), "transformType" : TransformType.TRANSLATION_ENTITY, "oppositeDirectionEntity" : false, "transformLine" : qUnion([Q1]), "makeCopy" : false});
        }
        {
            var Q0;
            Q0=qCreatedBy(makeId("Front.planeOp"),FACE);
            var sketch = newSketch(context, id + "F24", { "sketchPlane" : qUnion([Q0])});
            skCircle(sketch, "E45", {"center": v(-27.02, 0) * mm, "radius": 9.11 * mm});
            skCircle(sketch, "E46.MirrorC", {"center": v(27.02, 0) * mm, "radius": 9.11 * mm});
            skSolve(sketch);
        }
        {
            var Q0;
            Q0=qSketchRegion(id+"F24",true);
            extrude(context, id + "F25", {"entities" : qUnion([Q0]), "operationType" : NewBodyOperationType.REMOVE, "endBound" : BoundingType.SYMMETRIC, "depth" : 30 * mm});
        }
        {
            var Q0;
            Q0=makeQuery(id+"F1.opExtrude","SWEPT_FACE",FACE,{"disambiguationData":[OSD([sQuery(id+"F0.wireOp",EDGE,"E0"),sQuery(id+"F0.wireOp",EDGE,"E2")])]});
            var Q1;
            Q1=makeQuery(id+"F1.opExtrude","SWEPT_FACE",FACE,{"disambiguationData":[OSD([sQuery(id+"F0.wireOp",EDGE,"E1")])]});
            fillet(context, id + "F26", {"entities" : qUnion([Q0, Q1]), "radius" : 0.5 * mm, "tangentPropagation" : true, "allowEdgeOverflow" : false});
        }
    });
